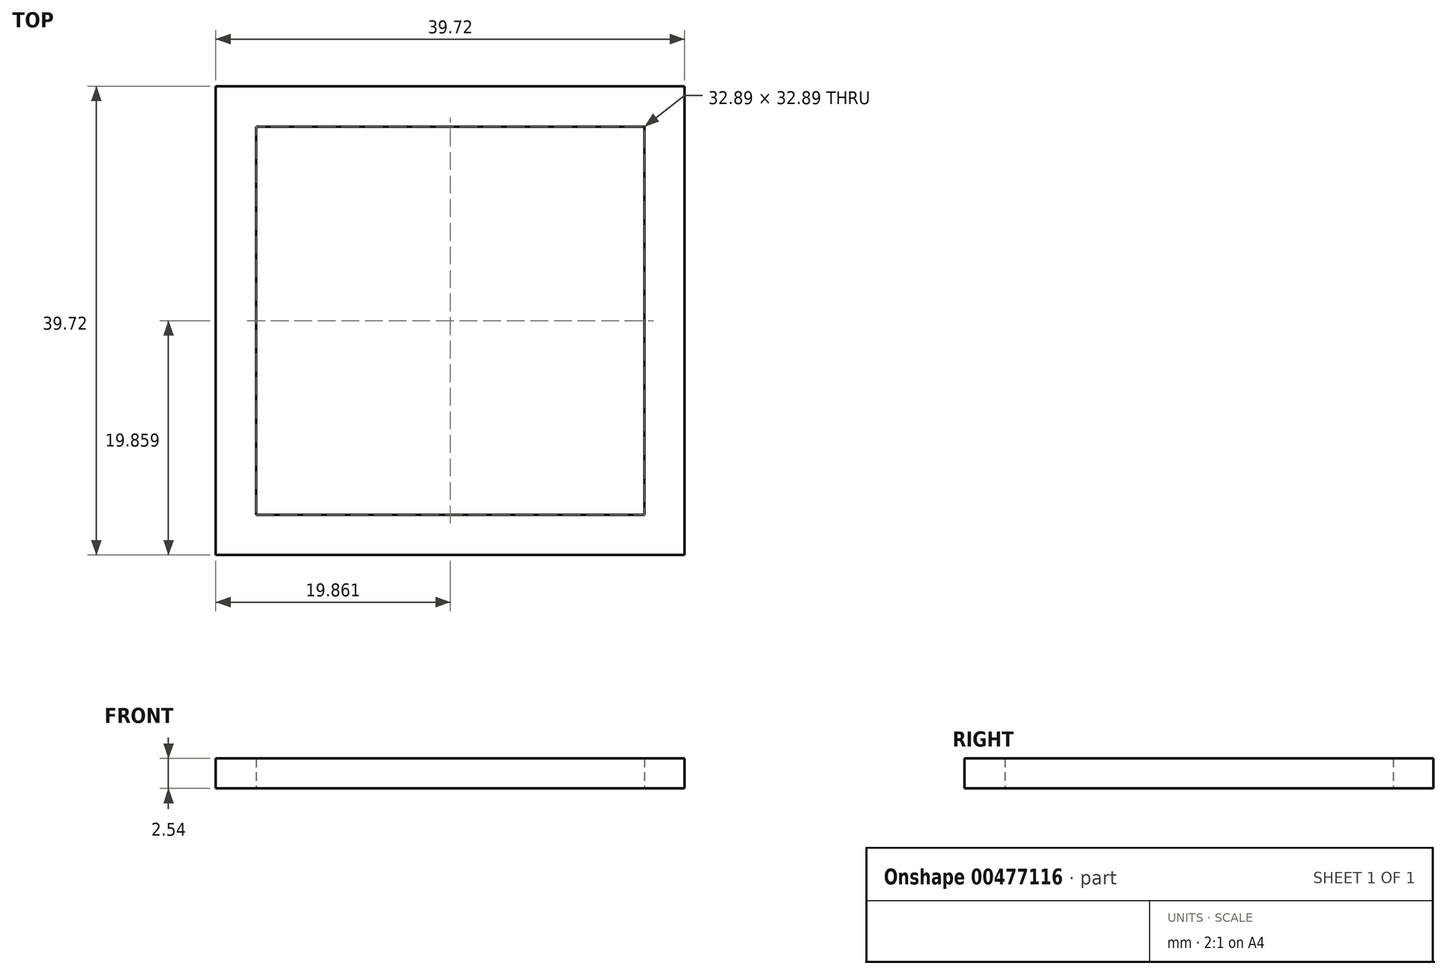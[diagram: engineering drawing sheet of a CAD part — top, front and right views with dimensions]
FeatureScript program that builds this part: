
annotation { "Feature Type Name" : "Feature", "Feature Type Description" : "" }
export const myFeature = defineFeature(function(context is Context, id is Id, definition is map)
    precondition{}
    {
        {
            var Q0;
            Q0=qCreatedBy(makeId("Top.planeOp"),FACE);
            var sketch = newSketch(context, id + "F0", { "sketchPlane" : qUnion([Q0])});
            skLineSegment(sketch, "E0.bottom", {"start": v(0, 0) * mm, "end": v(-39.72, 0) * mm});
            skLineSegment(sketch, "E0.top", {"start": v(0, 39.72) * mm, "end": v(-39.72, 39.72) * mm});
            skLineSegment(sketch, "E0.left", {"start": v(0, 0) * mm, "end": v(0, 39.72) * mm});
            skLineSegment(sketch, "E0.right", {"start": v(-39.72, 0) * mm, "end": v(-39.72, 39.72) * mm});
            skLineSegment(sketch, "E1", {"start": v(-3.41, 3.41) * mm, "end": v(-3.41, 36.3) * mm});
            skLineSegment(sketch, "E2", {"start": v(-36.3, 3.41) * mm, "end": v(-3.41, 3.41) * mm});
            skPoint(sketch, "E3.center.orphan", {"position": v(-19.86, 19.86) * mm});
            skLineSegment(sketch, "E4.trimOffspring", {"start": v(-36.3, 36.3) * mm, "end": v(-3.41, 36.3) * mm});
            skLineSegment(sketch, "E5.trimOffspring", {"start": v(-36.3, 3.41) * mm, "end": v(-36.3, 36.3) * mm});
            skSolve(sketch);
        }
        {
            var Q0;
            Q0 = qSketchRegion(id + "F0", true);
            extrude(context, id + "F1", {"entities" : qUnion([Q0]), "depth" : 2.54 * mm});
        }
    });
